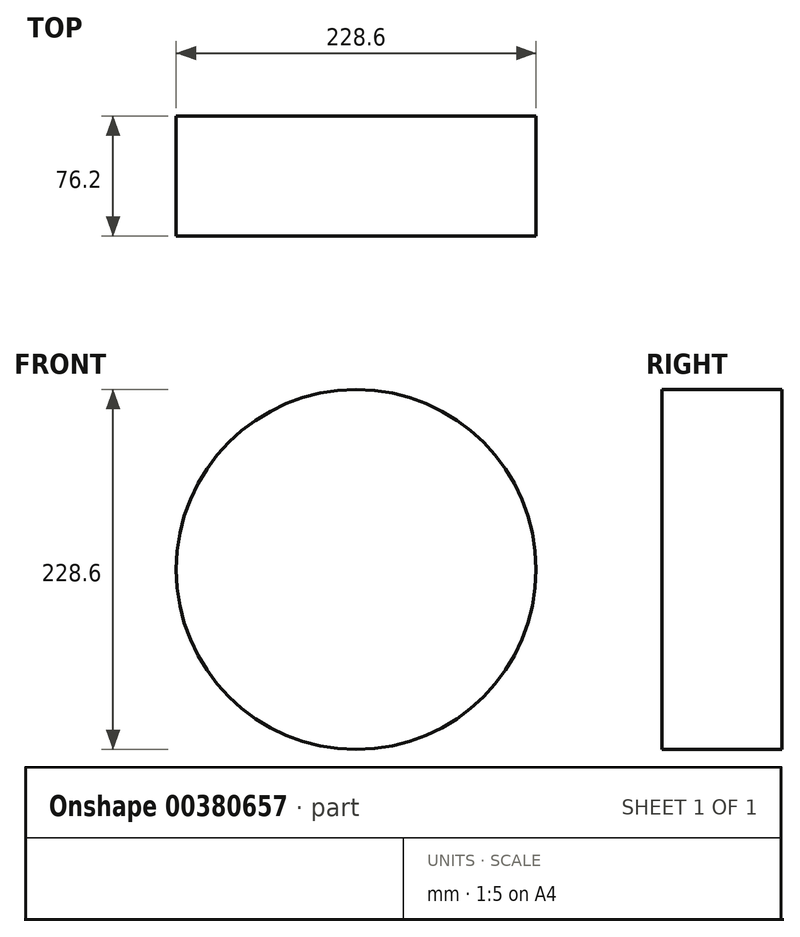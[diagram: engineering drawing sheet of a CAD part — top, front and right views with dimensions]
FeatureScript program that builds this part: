
annotation { "Feature Type Name" : "Feature", "Feature Type Description" : "" }
export const myFeature = defineFeature(function(context is Context, id is Id, definition is map)
    precondition{}
    {
        {
            var Q0;
            Q0=qCreatedBy(makeId("Front.planeOp"),FACE);
            var sketch = newSketch(context, id + "F0", { "sketchPlane" : qUnion([Q0])});
            skCircle(sketch, "E0", {"center": v(0, 0) * mm, "radius": 114.3 * mm});
            skSolve(sketch);
        }
        {
            var Q0;
            Q0=makeQuery(id+"F0.imprint","IMPRINT",FACE,{"disambiguationData":[TD([[makeQuery(id+"F0.imprint","IMPRINT",EDGE,{"derivedFrom":sQuery(id+"F0.wireOp",EDGE,"E0")}),1.0]])]});
            extrude(context, id + "F1", {"entities" : qUnion([Q0]), "oppositeDirection" : true, "depth" : 76.2 * mm});
        }
    });
